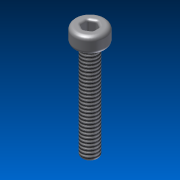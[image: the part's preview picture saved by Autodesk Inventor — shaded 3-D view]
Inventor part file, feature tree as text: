
AUTODESK INVENTOR PART (.ipt)
format: ipt  version: 2013 (Build 170138000, 138)  size: 158,208 bytes
history: native  units: mm
features: extrude x3, sketch x3, fillet x2, other x1, thread x1
ambient origin geometry x1: Origin
feature tree (10):
  other  "ソリッド1"
  extrude  "押し出し1"  Depth=3.8mm
  extrude  "押し出し2"  Depth=2.0mm TaperAngle=0.0deg
  extrude  "押し出し3"  Depth=2.0mm
  fillet  "フィレット1"  Radius=12.0mm
  fillet  "フィレット2"  Radius=0.75mm
  thread  "ねじ3"
  sketch  "スケッチ1"
  sketch  "スケッチ2"
  sketch  "スケッチ3"
